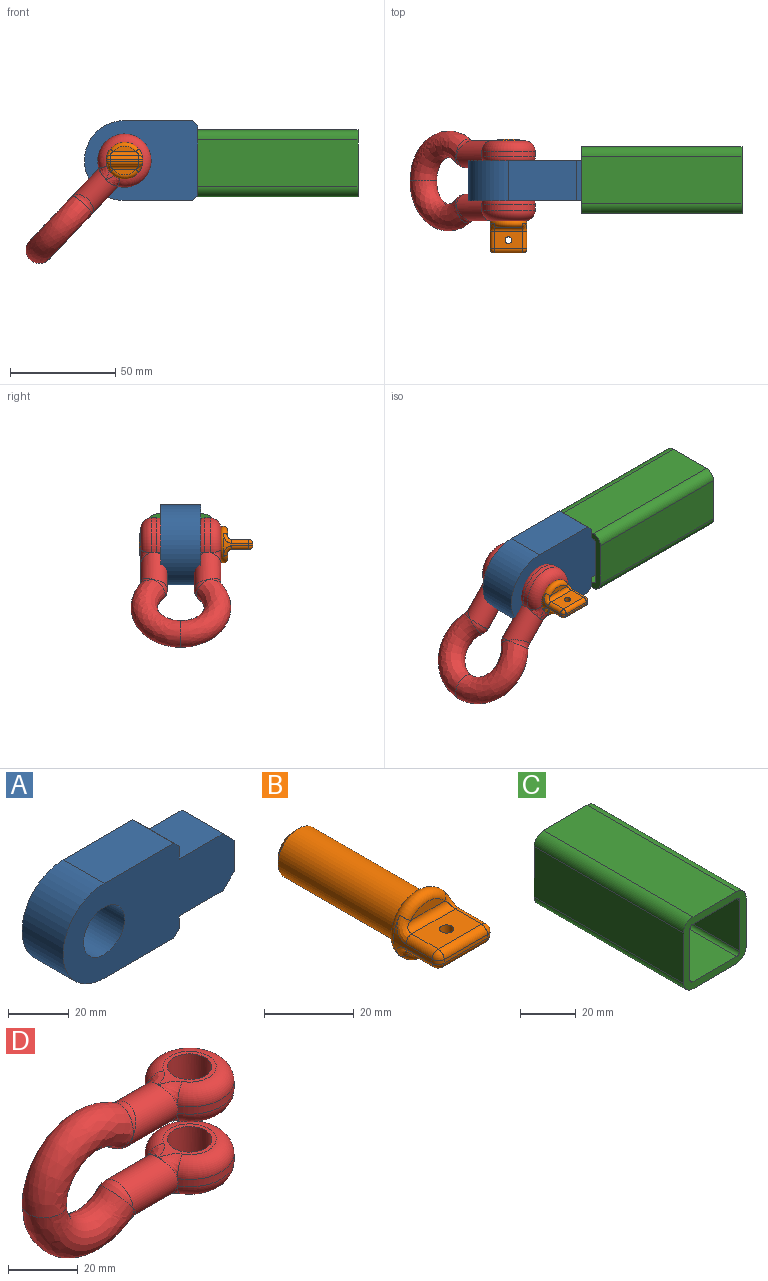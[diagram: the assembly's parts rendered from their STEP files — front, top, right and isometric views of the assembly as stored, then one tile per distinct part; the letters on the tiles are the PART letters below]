
ASSEMBLY  parts=4 mates=4
PART A: 15 faces, bbox 79.4x19.1x38.1 mm
  f0: plane 32.39x19.05mm, normal (0,0,1), area 616.9mm2, adj f1,f9,f10,f11
  f1: cylinder r=19.05mm len=38.1mm, axis (0,1,0), area 1140.1mm2, adj f0,f2,f9,f10
  f2: plane 32.39x19.05mm, normal (0,0,-1), area 616.9mm2, adj f1,f9,f10,f12
  f3: plane 19.05x5.08mm, normal (1,0,0), area 96.8mm2, adj f4,f9,f10,f12
  f4: plane 20.32x19.05mm, normal (0,0,-1), area 387.1mm2, adj f3,f9,f10,f14
  f5: plane 19.05x12.7mm, normal (1,0,0), area 241.9mm2, adj f9,f10,f13,f14
  f6: plane 20.32x19.05mm, normal (0,0,1), area 387.1mm2, adj f7,f9,f10,f13
  f7: plane 19.05x5.08mm, normal (1,0,0), area 96.8mm2, adj f6,f9,f10,f11
  f8: cylinder r=9.53mm len=19.05mm, axis (0,1,0), area 1140.1mm2, adj f9,f10
  f9: plane 79.38x38.1mm, normal (0,-1,0), area 2164.1mm2, adj f0,f1,f2,f3,f4,f5,f6,f7
  f10: plane 79.38x38.1mm, normal (0,1,0), area 2164.1mm2, adj f0,f1,f2,f3,f4,f5,f6,f7
  f11: plane 19.05x2.54mm, normal (0.71,0,0.71), area 68.4mm2, adj f0,f7,f9,f10
  f12: plane 19.05x2.54mm, normal (0.71,0,-0.71), area 68.4mm2, adj f2,f3,f9,f10
  f13: plane 19.05x5.08mm, normal (0.71,0,0.71), area 136.9mm2, adj f5,f6,f9,f10
  f14: plane 19.05x5.08mm, normal (0.71,0,-0.71), area 136.9mm2, adj f4,f5,f9,f10
PART B: 31 faces, bbox 18.9x54x18.9 mm
  f0: cylinder r=8.73mm len=12.07mm, axis (0,1,0), area 22.9mm2, adj f11,f14,f15,f18,f19,f22
  f1: cylinder r=8.73mm len=12.07mm, axis (0,1,0), area 22.9mm2, adj f13,f17,f18,f24,f27,f28
  f2: plane 13.65x0.95mm, normal (0,-1,0), area 13mm2, adj f15,f16,f23,f24
  f3: cylinder r=6.35mm len=36.83mm, axis (0,1,0), area 1469.5mm2, adj f5,f29
  f4: plane 10.16x10.16mm, normal (0,1,0), area 81.1mm2, adj f29
  f5: plane 13.65x13.65mm, normal (0,1,0), area 19.7mm2, adj f3,f18
  f6: plane 10.63x2.54mm, normal (0,-1,0), area 18.8mm2, adj f10,f18
  f7: plane 13.62x8.26mm, normal (0,0,1), area 104.5mm2, adj f10,f11,f16,f17,f30
  f8: plane 10.63x2.54mm, normal (0,-1,0), area 18.8mm2, adj f18,f25
  f9: plane 13.62x8.26mm, normal (0,0,-1), area 104.5mm2, adj f19,f23,f25,f28,f30
  f10: cylinder r=1.91mm len=13.62mm, axis (-1,0,0), area 38.6mm2, adj f6,f7,f13,f14
  f11: cylinder r=1.91mm len=8.26mm, axis (0,1,0), area 23.6mm2, adj f0,f7,f12,f14
  f12: sphere r=1.91mm, area 5.5mm2, adj f11,f15,f16
  f13: bspline ~6.06x4.29mm, area 14.2mm2, adj f1,f10,f17,f18
  f14: bspline ~5.86x4.67mm, area 14.2mm2, adj f0,f10,f11,f18
  f15: torus R=6.83mm, axis (0,-1,0), area 3.4mm2, adj f0,f2,f12,f20
  f16: cylinder r=1.91mm len=13.62mm, axis (1,0,0), area 40.8mm2, adj f2,f7,f12,f21
  f17: cylinder r=1.91mm len=8.26mm, axis (0,1,0), area 23.6mm2, adj f1,f7,f13,f21
  f18: torus R=6.83mm, axis (0,-1,0), area 237mm2, adj f0,f1,f5,f6,f8,f13,f14,f22
  f19: cylinder r=1.91mm len=8.26mm, axis (0,1,0), area 23.6mm2, adj f0,f9,f20,f22
  f20: sphere r=1.91mm, area 5.5mm2, adj f15,f19,f23
  f21: sphere r=1.91mm, area 5.4mm2, adj f16,f17,f24
  f22: bspline ~6.06x4.29mm, area 14.2mm2, adj f0,f18,f19,f25
  f23: cylinder r=1.91mm len=13.62mm, axis (-1,0,0), area 40.8mm2, adj f2,f9,f20,f26
  f24: torus R=6.83mm, axis (0,-1,0), area 3.4mm2, adj f1,f2,f21,f26
  f25: cylinder r=1.91mm len=13.62mm, axis (-1,0,0), area 38.6mm2, adj f8,f9,f22,f27
  f26: sphere r=1.91mm, area 5.4mm2, adj f23,f24,f28
  f27: bspline ~5.86x4.67mm, area 14.2mm2, adj f1,f18,f25,f28
  f28: cylinder r=1.91mm len=8.26mm, axis (0,1,0), area 23.6mm2, adj f1,f9,f26,f27
  f29: cone r=6.35mm half-angle=45deg, axis (0,-1,0), area 64.5mm2, adj f3,f4
  f30: cylinder r=1.59mm len=4.76mm, axis (0,0,-1), area 47.5mm2, adj f7,f9
PART C: 18 faces, bbox 31.8x76.2x31.8 mm
  f0: plane 76.2x22.23mm, normal (-1,0,0), area 1693.5mm2, adj f1,f15,f16,f17
  f1: cylinder r=4.76mm len=76.2mm, axis (0,1,0), area 570mm2, adj f0,f2,f16,f17
  f2: plane 76.2x22.23mm, normal (0,0,-1), area 1693.5mm2, adj f1,f3,f16,f17
  f3: cylinder r=4.76mm len=76.2mm, axis (0,1,0), area 570mm2, adj f2,f4,f16,f17
  f4: plane 76.2x22.23mm, normal (1,0,0), area 1693.5mm2, adj f3,f5,f16,f17
  f5: cylinder r=4.76mm len=76.2mm, axis (0,1,0), area 570mm2, adj f4,f6,f16,f17
  f6: plane 76.2x22.23mm, normal (0,0,1), area 1693.5mm2, adj f5,f15,f16,f17
  f7: cylinder r=1.59mm len=76.2mm, axis (0,1,0), area 190mm2, adj f8,f14,f16,f17
  f8: plane 76.2x22.23mm, normal (-1,0,0), area 1693.5mm2, adj f7,f9,f16,f17
  f9: cylinder r=1.59mm len=76.2mm, axis (0,1,0), area 190mm2, adj f8,f10,f16,f17
  f10: plane 76.2x22.23mm, normal (0,0,1), area 1693.5mm2, adj f9,f11,f16,f17
  f11: cylinder r=1.59mm len=76.2mm, axis (0,1,0), area 190mm2, adj f10,f12,f16,f17
  f12: plane 76.2x22.23mm, normal (1,0,0), area 1693.5mm2, adj f11,f13,f16,f17
  f13: cylinder r=1.59mm len=76.2mm, axis (0,1,0), area 190mm2, adj f12,f14,f16,f17
  f14: plane 76.2x22.23mm, normal (0,0,-1), area 1693.5mm2, adj f7,f13,f16,f17
  f15: cylinder r=4.76mm len=76.2mm, axis (0,1,0), area 570mm2, adj f0,f6,f16,f17
  f16: plane 31.75x31.75mm, normal (0,-1,0), area 345.6mm2, adj f0,f1,f2,f3,f4,f5,f6,f7
  f17: plane 31.75x31.75mm, normal (0,1,0), area 345.6mm2, adj f0,f1,f2,f3,f4,f5,f6,f7
PART D: 28 faces, bbox 78.8x27.5x48 mm
  f0: cylinder r=12.7mm len=25.4mm, axis (0,0,-1), area 169.2mm2, adj f4,f11,f20
  f1: cylinder r=12.7mm len=25.4mm, axis (0,0,-1), area 169.2mm2, adj f5,f14,f17
  f2: plane 20.32x15.24mm, normal (0,0,1), area 67.3mm2, adj f19,f20,f21,f26
  f3: plane 20.32x15.24mm, normal (0,0,-1), area 67.3mm2, adj f16,f17,f18,f27
  f4: cylinder r=6.35mm len=18.55mm, axis (1,0,0), area 649.4mm2, adj f0,f10,f12,f19,f21,f22,f23
  f5: cylinder r=6.35mm len=18.55mm, axis (-1,0,0), area 649.4mm2, adj f1,f13,f15,f16,f18,f24,f25
  f6: bspline ~40.81x25.4mm, area 1582mm2, adj f7,f22,f23
  f7: bspline ~40.81x25.4mm, area 1581.8mm2, adj f6,f24,f25
  f8: plane 20.32x15.24mm, normal (0,0,1), area 67.3mm2, adj f13,f14,f15,f27
  f9: plane 20.32x15.24mm, normal (0,0,-1), area 67.3mm2, adj f10,f11,f12,f26
  f10: bspline ~6.45x6.32mm, area 15.1mm2, adj f4,f9,f11
  f11: torus R=7.62mm, axis (0,0,-1), area 455.5mm2, adj f0,f9,f10,f12
  f12: bspline ~6.32x6.29mm, area 15.1mm2, adj f4,f9,f11
  f13: bspline ~6.32x6.29mm, area 15.1mm2, adj f5,f8,f14
  f14: torus R=7.62mm, axis (0,0,-1), area 455.5mm2, adj f1,f8,f13,f15
  f15: bspline ~6.45x6.32mm, area 15.1mm2, adj f5,f8,f14
  f16: bspline ~6.32x6.29mm, area 15.1mm2, adj f3,f5,f17
  f17: torus R=7.62mm, axis (0,0,1), area 455.5mm2, adj f1,f3,f16,f18
  f18: bspline ~6.45x6.32mm, area 15.1mm2, adj f3,f5,f17
  f19: bspline ~6.45x6.32mm, area 15.1mm2, adj f2,f4,f20
  f20: torus R=7.62mm, axis (0,0,1), area 455.5mm2, adj f0,f2,f19,f21
  f21: bspline ~6.32x6.29mm, area 15.1mm2, adj f2,f4,f20
  f22: bspline ~12.7x7.19mm, area 39.5mm2, adj f4,f6
  f23: bspline ~12.7x6.36mm, area 28.1mm2, adj f4,f6
  f24: bspline ~12.7x7.19mm, area 39.5mm2, adj f5,f7
  f25: bspline ~12.7x6.36mm, area 28.1mm2, adj f5,f7
  f26: cylinder r=6.35mm len=12.7mm, axis (0,0,-1), area 506.7mm2, adj f2,f9
  f27: cylinder r=6.35mm len=12.7mm, axis (0,0,-1), area 506.7mm2, adj f3,f8
PLACE A t=(-86.43,39.35,-34.68)mm fixed
PLACE B t=(-86.43,49.51,-34.68)mm
PLACE C rot(axis=(0,0,1),90deg) t=(-51.5,30.13,-35.95)mm
PLACE D rot(axis=(0.86,-0.37,0.37),98.9deg) t=(-114.88,29.82,-64.57)mm
MATE revolute D.f26 <-> A.f8  axis (0,-1,0) through (-86.43,36.17,-34.68)mm
MATE slider B.f3 <-> A.f1  axis (0,1,0) through (-86.43,29.82,-34.68)mm
MATE planar A.f6 <-> C.f14  axis (0,0,1) through (-41.34,29.82,-23.25)mm
MATE planar A.f3 <-> C.f17  axis (1,0,0) through (-51.5,29.82,-48.65)mm
